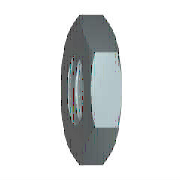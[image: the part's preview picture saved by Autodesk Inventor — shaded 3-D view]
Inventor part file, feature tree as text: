
AUTODESK INVENTOR PART (.ipt)
format: ipt  version: 2019 (Build 230136000, 136)  size: 163,840 bytes
history: native  units: mm (DEFAULTED — no unit token found)
features: sketch x3, other x2, extrude x1, hole x1, plane x1
ambient origin geometry x7: Origin, YZ Plane, XZ Plane, X Axis, Y Axis, Z Axis, Center Point
bodies: Body1 (feature_tree)
feature tree (8):
  extrude  "Базовый элемент"  Depth=20.78461mm
  other  "Фаска1"
  hole  "Резьба"  [1 undecoded]
  other  "Work Axis1"
  plane  "Work Plane1"
  sketch  "Эскиз1"
  sketch  "Эскиз2"
  sketch  "Эскиз3"
note: 1 required parameter value undecoded (feature->parameter linkage not recoverable at this tier; creation-order binding heuristic only, values carry confidence <= 0.55)
